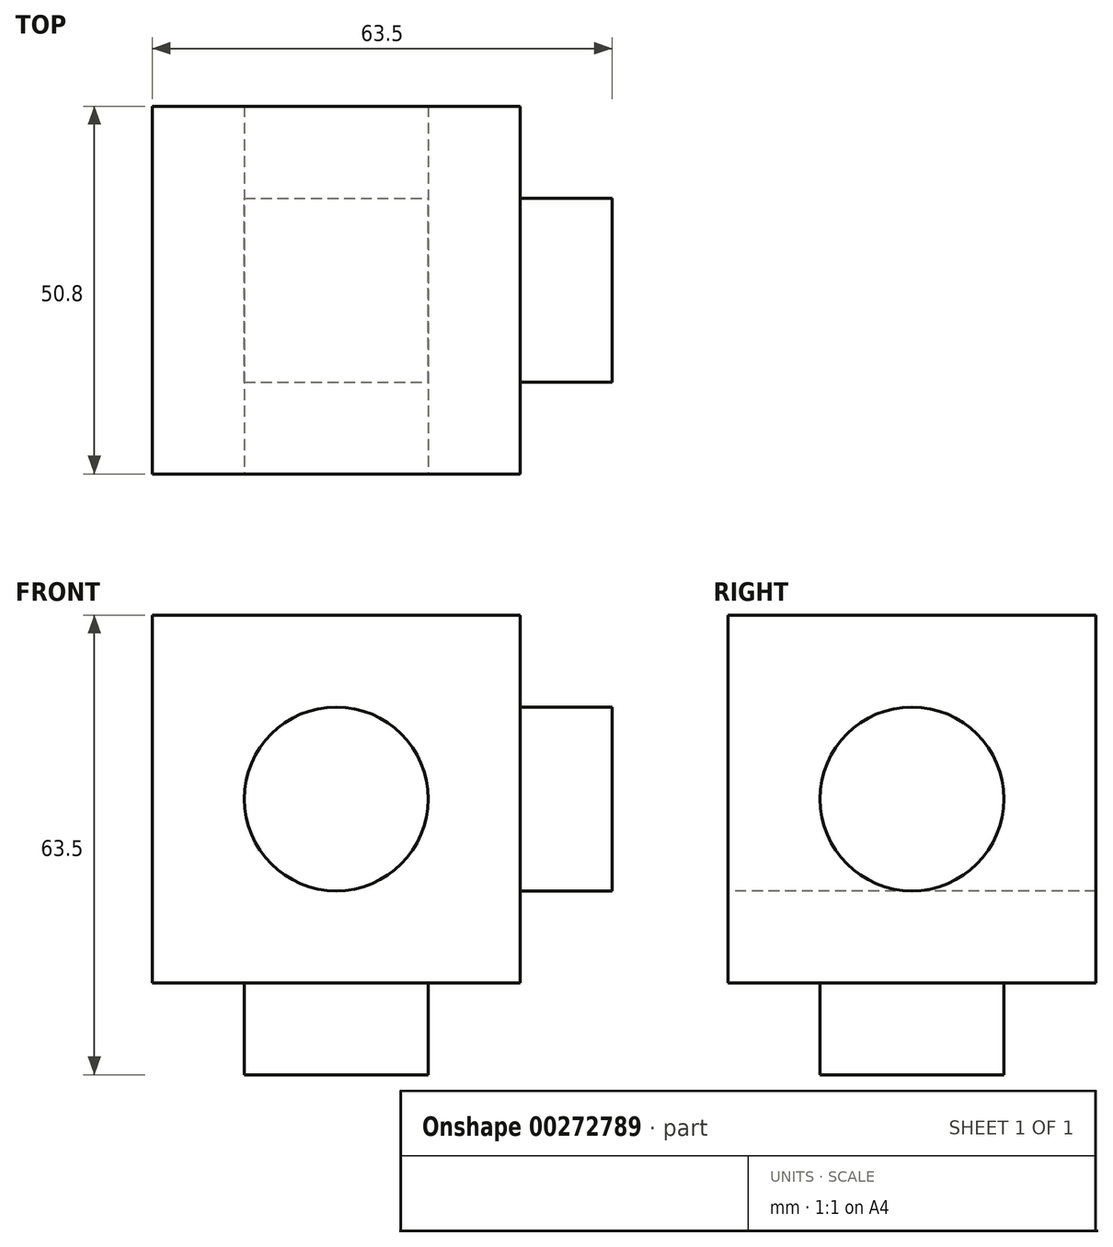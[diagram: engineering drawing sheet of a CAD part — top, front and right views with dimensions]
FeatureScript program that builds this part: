
annotation { "Feature Type Name" : "Feature", "Feature Type Description" : "" }
export const myFeature = defineFeature(function(context is Context, id is Id, definition is map)
    precondition{}
    {
        {
            var Q0;
            Q0=qCreatedBy(makeId("Front.planeOp"),FACE);
            var sketch = newSketch(context, id + "F0", { "sketchPlane" : qUnion([Q0])});
            skLineSegment(sketch, "E0.bottom", {"start": v(0, 0) * mm, "end": v(-50.8, 0) * mm});
            skLineSegment(sketch, "E0.top", {"start": v(0, 50.8) * mm, "end": v(-50.8, 50.8) * mm});
            skLineSegment(sketch, "E0.left", {"start": v(0, 0) * mm, "end": v(0, 50.8) * mm});
            skLineSegment(sketch, "E0.right", {"start": v(-50.8, 0) * mm, "end": v(-50.8, 50.8) * mm});
            skSolve(sketch);
        }
        {
            var Q0;
            Q0 = qSketchRegion(id + "F0", true);
            extrude(context, id + "F1", {"entities" : qUnion([Q0]), "depth" : 50.8 * mm});
        }
        {
            var Q0;
            Q0=makeQuery(id+"F1.opExtrude","CAP_FACE",FACE,{"disambiguationData":[OSD([sQuery(id+"F0.wireOp",EDGE,"E0.bottom"),sQuery(id+"F0.wireOp",EDGE,"E0.top"),sQuery(id+"F0.wireOp",EDGE,"E0.left"),sQuery(id+"F0.wireOp",EDGE,"E0.right")])],"isStart":false});
            var sketch = newSketch(context, id + "F2", { "sketchPlane" : qUnion([Q0])});
            skCircle(sketch, "E1", {"center": v(-25.4, 25.4) * mm, "radius": 12.7 * mm});
            skSolve(sketch);
        }
        {
            var Q0;
            Q0 = qSketchRegion(id + "F2", true);
            extrude(context, id + "F3", {"entities" : qUnion([Q0]), "operationType" : NewBodyOperationType.REMOVE, "oppositeDirection" : true, "depth" : 50.8 * mm});
        }
        {
            var Q0;
            Q0=makeQuery(id+"F1.opExtrude","SWEPT_FACE",FACE,{"disambiguationData":[OSD([sQuery(id+"F0.wireOp",EDGE,"E0.left")])]});
            var sketch = newSketch(context, id + "F4", { "sketchPlane" : qUnion([Q0])});
            skCircle(sketch, "E2", {"center": v(-25.4, 25.4) * mm, "radius": 12.7 * mm});
            skSolve(sketch);
        }
        {
            var Q0;
            Q0 = qSketchRegion(id + "F4", true);
            extrude(context, id + "F5", {"entities" : qUnion([Q0]), "operationType" : NewBodyOperationType.ADD, "depth" : 12.7 * mm});
        }
        {
            var Q0;
            Q0=makeQuery(id+"F1.opExtrude","SWEPT_FACE",FACE,{"disambiguationData":[OSD([sQuery(id+"F0.wireOp",EDGE,"E0.bottom")])]});
            var sketch = newSketch(context, id + "F6", { "sketchPlane" : qUnion([Q0])});
            skLineSegment(sketch, "E3.bottom", {"start": v(-38.1, 38.1) * mm, "end": v(-12.7, 38.1) * mm});
            skLineSegment(sketch, "E3.top", {"start": v(-38.1, 12.7) * mm, "end": v(-12.7, 12.7) * mm});
            skLineSegment(sketch, "E3.left", {"start": v(-38.1, 38.1) * mm, "end": v(-38.1, 12.7) * mm});
            skLineSegment(sketch, "E3.right", {"start": v(-12.7, 38.1) * mm, "end": v(-12.7, 12.7) * mm});
            skSolve(sketch);
        }
        {
            var Q0;
            Q0 = qSketchRegion(id + "F6", true);
            extrude(context, id + "F7", {"entities" : qUnion([Q0]), "operationType" : NewBodyOperationType.ADD, "depth" : 12.7 * mm});
        }
    });
